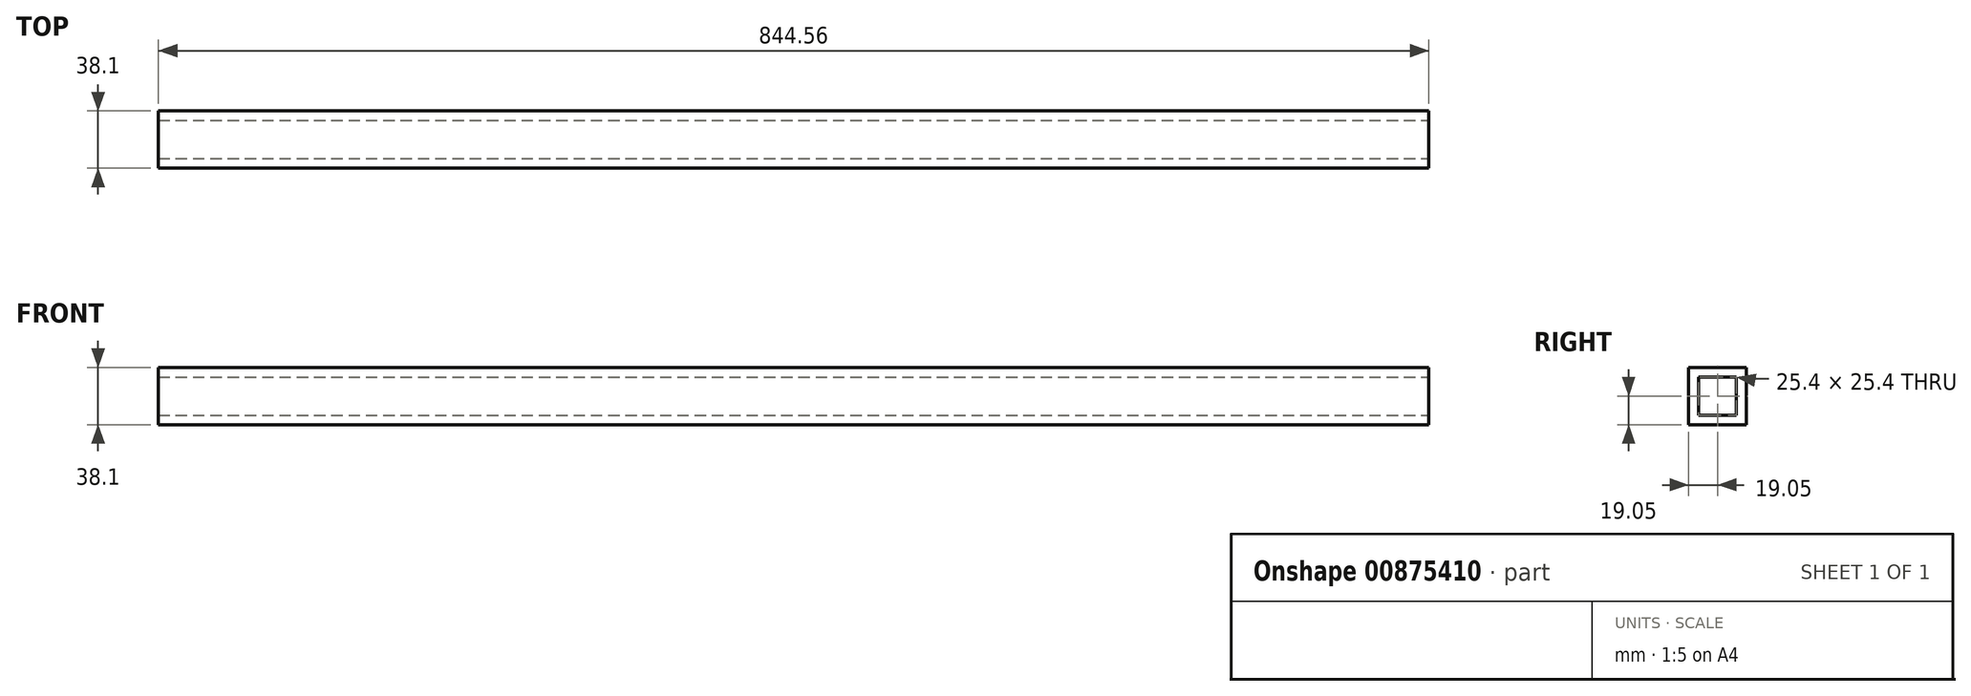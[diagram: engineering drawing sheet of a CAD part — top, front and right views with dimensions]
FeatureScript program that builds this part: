
annotation { "Feature Type Name" : "Feature", "Feature Type Description" : "" }
export const myFeature = defineFeature(function(context is Context, id is Id, definition is map)
    precondition{}
    {
        {
            var Q0;
            Q0=qCreatedBy(makeId("Front.planeOp"),FACE);
            var sketch = newSketch(context, id + "F0", { "sketchPlane" : qUnion([Q0])});
            skLineSegment(sketch, "E0.bottom", {"start": v(422.28, 19.05) * mm, "end": v(-422.28, 19.05) * mm});
            skLineSegment(sketch, "E0.top", {"start": v(422.28, -19.05) * mm, "end": v(-422.28, -19.05) * mm});
            skLineSegment(sketch, "E0.left", {"start": v(422.28, 19.05) * mm, "end": v(422.28, -19.05) * mm});
            skLineSegment(sketch, "E0.right", {"start": v(-422.28, 19.05) * mm, "end": v(-422.28, -19.05) * mm});
            skPoint(sketch, "E0.middle", {"position": v(0, 0) * mm});
            skSolve(sketch);
        }
        {
            var Q0;
            Q0=makeQuery(id+"F0.imprint","IMPRINT",FACE,{"disambiguationData":[TD([[makeQuery(id+"F0.imprint","IMPRINT",EDGE,{"derivedFrom":sQuery(id+"F0.wireOp",EDGE,"E0.bottom")}),1.0]])]});
            extrude(context, id + "F1", {"entities" : qUnion([Q0]), "depth" : 38.1 * mm, "offsetDistance" : 25.4 * mm});
        }
        {
            var Q0;
            Q0=makeQuery(id+"F1.opExtrude","SWEPT_FACE",FACE,{"disambiguationData":[OSD([sQuery(id+"F0.wireOp",EDGE,"E0.left")])]});
            var sketch = newSketch(context, id + "F2", { "sketchPlane" : qUnion([Q0])});
            skLineSegment(sketch, "E1.bottom", {"start": v(-6.35, 12.7) * mm, "end": v(-31.75, 12.7) * mm});
            skLineSegment(sketch, "E1.top", {"start": v(-6.35, -12.7) * mm, "end": v(-31.75, -12.7) * mm});
            skLineSegment(sketch, "E1.left", {"start": v(-6.35, 12.7) * mm, "end": v(-6.35, -12.7) * mm});
            skLineSegment(sketch, "E1.right", {"start": v(-31.75, 12.7) * mm, "end": v(-31.75, -12.7) * mm});
            skPoint(sketch, "E1.middle", {"position": v(-19.05, 0) * mm});
            skPoint(sketch, "E1.middle.positionSnap0", {"position": v(-19.05, 19.05) * mm});
            skPoint(sketch, "E1.centerSnap0", {"position": v(-19.05, 19.05) * mm});
            skSolve(sketch);
        }
        {
            var Q0;
            Q0=makeQuery(id+"F2.imprint","IMPRINT",FACE,{"disambiguationData":[TD([[makeQuery(id+"F2.imprint","IMPRINT",EDGE,{"derivedFrom":sQuery(id+"F2.wireOp",EDGE,"E1.bottom")}),1.0]])]});
            extrude(context, id + "F3", {"entities" : qUnion([Q0]), "operationType" : NewBodyOperationType.REMOVE, "endBound" : BoundingType.THROUGH_ALL, "oppositeDirection" : true, "depth" : 25.4 * mm, "offsetDistance" : 25.4 * mm});
        }
    });
